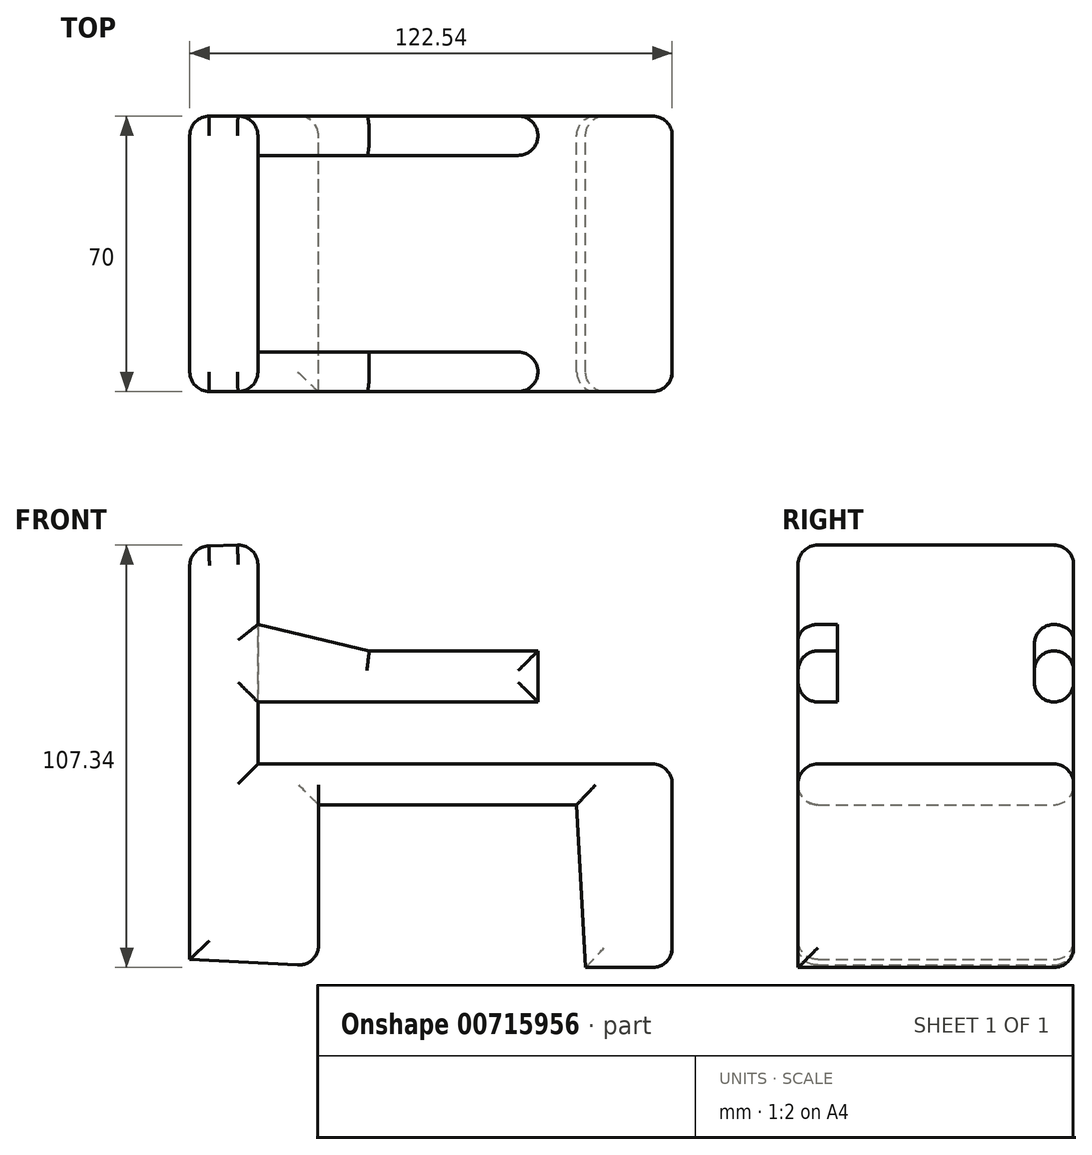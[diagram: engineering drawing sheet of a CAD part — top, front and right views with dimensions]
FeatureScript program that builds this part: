
annotation { "Feature Type Name" : "Feature", "Feature Type Description" : "" }
export const myFeature = defineFeature(function(context is Context, id is Id, definition is map)
    precondition{}
    {
        {
            var Q0;
            Q0=qCreatedBy(makeId("Front.planeOp"),FACE);
            var sketch = newSketch(context, id + "F0", { "sketchPlane" : qUnion([Q0])});
            skLineSegment(sketch, "E0", {"start": v(-51.51, 44.26) * mm, "end": v(-51.51, -11.56) * mm});
            skLineSegment(sketch, "E1", {"start": v(-51.51, -11.56) * mm, "end": v(53.74, -11.56) * mm});
            skLineSegment(sketch, "E2", {"start": v(53.74, -11.56) * mm, "end": v(53.74, -63.24) * mm});
            skLineSegment(sketch, "E3", {"start": v(53.74, -63.24) * mm, "end": v(31.75, -63.24) * mm});
            skLineSegment(sketch, "E4", {"start": v(31.75, -63.24) * mm, "end": v(29.5, -21.9) * mm});
            skLineSegment(sketch, "E5", {"start": v(29.5, -21.9) * mm, "end": v(-36.1, -21.9) * mm});
            skLineSegment(sketch, "E6", {"start": v(-36.1, -21.9) * mm, "end": v(-36.1, -62.87) * mm});
            skLineSegment(sketch, "E7", {"start": v(-36.1, -62.87) * mm, "end": v(-68.8, -61.18) * mm});
            skLineSegment(sketch, "E8", {"start": v(-68.8, -61.18) * mm, "end": v(-68.8, 43.7) * mm});
            skLineSegment(sketch, "E9", {"start": v(-68.8, 43.7) * mm, "end": v(-51.51, 44.26) * mm});
            skSolve(sketch);
        }
        {
            var Q0;
            Q0 = qSketchRegion(id + "F0", true);
            extrude(context, id + "F1", {"entities" : qUnion([Q0]), "depth" : 70 * mm, "offsetDistance" : 25 * mm});
        }
        {
            var Q0;
            Q0=qCreatedBy(makeId("Front.planeOp"),FACE);
            cPlane(context, id + "F2", {"entities" : qUnion([Q0]), "cplaneType" : CPlaneType.OFFSET, "offset" : 35 * mm, "width" : 150 * mm, "height" : 150 * mm});
        }
        {
            var Q0;
            Q0=qCreatedBy(makeId("Front.planeOp"),FACE);
            var sketch = newSketch(context, id + "F3", { "sketchPlane" : qUnion([Q0])});
            skLineSegment(sketch, "E10", {"start": v(-56.48, 25.1) * mm, "end": v(-23.21, 17.2) * mm});
            skLineSegment(sketch, "E11", {"start": v(-23.21, 17.2) * mm, "end": v(19.64, 17.2) * mm});
            skLineSegment(sketch, "E12", {"start": v(19.64, 17.2) * mm, "end": v(19.64, 4.23) * mm});
            skLineSegment(sketch, "E13", {"start": v(19.64, 4.23) * mm, "end": v(-56.48, 4.23) * mm});
            skLineSegment(sketch, "E14", {"start": v(-56.48, 4.23) * mm, "end": v(-56.48, 25.1) * mm});
            skSolve(sketch);
        }
        {
            var Q0;
            Q0 = qSketchRegion(id + "F3", true);
            extrude(context, id + "F4", {"entities" : qUnion([Q0]), "depth" : 10 * mm, "offsetDistance" : 25 * mm});
        }
        {
            var Q0;
            Q0=makeQuery(id+"F4.opExtrude","SWEPT_BODY",BODY,{"disambiguationData":[OSD([sQuery(id+"F3.wireOp",EDGE,"E10"),sQuery(id+"F3.wireOp",EDGE,"E11"),sQuery(id+"F3.wireOp",EDGE,"E12"),sQuery(id+"F3.wireOp",EDGE,"E13"),sQuery(id+"F3.wireOp",EDGE,"E14")])]});
            var Q1;
            Q1=qCreatedBy(id+"F2.planeOp",FACE);
            mirror(context, id + "F5", {"operationType" : NewBodyOperationType.ADD, "entities" : qUnion([Q0]), "mirrorPlane" : qUnion([Q1])});
        }
        {
            var Q0;
            Q0=makeQuery(id+"F1.opExtrude","CAP_EDGE",EDGE,{"disambiguationData":[OSD([sQuery(id+"F0.wireOp",EDGE,"E9")])],"isStart":true});
            var Q1;
            Q1=makeQuery(id+"F4.opExtrude","CAP_EDGE",EDGE,{"disambiguationData":[OSD([sQuery(id+"F3.wireOp",EDGE,"E10")])],"isStart":true});
            var Q2;
            Q2=makeQuery(id+"F4.opExtrude","CAP_EDGE",EDGE,{"disambiguationData":[OSD([sQuery(id+"F3.wireOp",EDGE,"E11")])],"isStart":true});
            var Q3;
            Q3=makeQuery(id+"F4.opExtrude","CAP_EDGE",EDGE,{"disambiguationData":[OSD([sQuery(id+"F3.wireOp",EDGE,"E12")])],"isStart":true});
            var Q4;
            Q4=makeQuery(id+"F4.opExtrude","CAP_EDGE",EDGE,{"disambiguationData":[OSD([sQuery(id+"F3.wireOp",EDGE,"E13")])],"isStart":true});
            var Q5;
            {var subQ0=sQuery(id+"F0.wireOp",EDGE,"E1");var subQ1=sQuery(id+"F0.wireOp",EDGE,"E0");Q5=makeQuery(id+"F5.boolean.opBoolean","SPLIT",EDGE,{"disambiguationData":[TD([makeQuery(id+"F1.opExtrude","SWEPT_FACE",FACE,{"disambiguationData":[OSD([subQ0])]})])],"derivedFrom":makeQuery(id+"F1.opExtrude","CAP_EDGE",EDGE,{"disambiguationData":[OSD([subQ1])],"isStart":true})});}
            var Q6;
            Q6=makeQuery(id+"F1.opExtrude","CAP_EDGE",EDGE,{"disambiguationData":[OSD([sQuery(id+"F0.wireOp",EDGE,"E1")])],"isStart":true});
            var Q7;
            Q7=makeQuery(id+"F1.opExtrude","CAP_EDGE",EDGE,{"disambiguationData":[OSD([sQuery(id+"F0.wireOp",EDGE,"E2")])],"isStart":true});
            var Q8;
            Q8=makeQuery(id+"F5.boolean.opBoolean","MERGE",FACE,{"derivedFrom":[makeQuery(id+"F1.opExtrude","CAP_FACE",FACE,{"disambiguationData":[OSD([sQuery(id+"F0.wireOp",EDGE,"E0"),sQuery(id+"F0.wireOp",EDGE,"E1"),sQuery(id+"F0.wireOp",EDGE,"E2"),sQuery(id+"F0.wireOp",EDGE,"E3"),sQuery(id+"F0.wireOp",EDGE,"E4"),sQuery(id+"F0.wireOp",EDGE,"E5"),sQuery(id+"F0.wireOp",EDGE,"E6"),sQuery(id+"F0.wireOp",EDGE,"E7"),sQuery(id+"F0.wireOp",EDGE,"E8"),sQuery(id+"F0.wireOp",EDGE,"E9")])],"isStart":true}),makeQuery(id+"F4.opExtrude","CAP_FACE",FACE,{"disambiguationData":[OSD([sQuery(id+"F3.wireOp",EDGE,"E10"),sQuery(id+"F3.wireOp",EDGE,"E11"),sQuery(id+"F3.wireOp",EDGE,"E12"),sQuery(id+"F3.wireOp",EDGE,"E13"),sQuery(id+"F3.wireOp",EDGE,"E14")])],"isStart":true})]});
            var Q9;
            Q9=makeQuery(id+"F1.opExtrude","CAP_EDGE",EDGE,{"disambiguationData":[OSD([sQuery(id+"F0.wireOp",EDGE,"E9")])],"isStart":false});
            var Q10;
            {var subQ0=sQuery(id+"F0.wireOp",EDGE,"E9");var subQ1=sQuery(id+"F0.wireOp",EDGE,"E0");Q10=makeQuery(id+"F5.boolean.opBoolean","SPLIT",EDGE,{"disambiguationData":[TD([makeQuery(id+"F1.opExtrude","SWEPT_FACE",FACE,{"disambiguationData":[OSD([subQ0])]})])],"derivedFrom":makeQuery(id+"F1.opExtrude","CAP_EDGE",EDGE,{"disambiguationData":[OSD([subQ1])],"isStart":false})});}
            var Q11;
            Q11=makeQuery(id+"F1.opExtrude","CAP_EDGE",EDGE,{"disambiguationData":[OSD([sQuery(id+"F0.wireOp",EDGE,"E8")])],"isStart":false});
            var Q12;
            Q12=makeQuery(id+"F1.opExtrude","CAP_EDGE",EDGE,{"disambiguationData":[OSD([sQuery(id+"F0.wireOp",EDGE,"E7")])],"isStart":false});
            var Q13;
            Q13=makeQuery(id+"F1.opExtrude","SWEPT_EDGE",EDGE,{"disambiguationData":[OSD([sQuery(id+"F0.wireOp",EDGE,"E6"),sQuery(id+"F0.wireOp",EDGE,"E7")])]});
            var Q14;
            Q14=makeQuery(id+"F1.opExtrude","CAP_EDGE",EDGE,{"disambiguationData":[OSD([sQuery(id+"F0.wireOp",EDGE,"E5")])],"isStart":false});
            var Q15;
            Q15=makeQuery(id+"F1.opExtrude","CAP_EDGE",EDGE,{"disambiguationData":[OSD([sQuery(id+"F0.wireOp",EDGE,"E4")])],"isStart":false});
            var Q16;
            Q16=makeQuery(id+"F1.opExtrude","SWEPT_EDGE",EDGE,{"disambiguationData":[OSD([sQuery(id+"F0.wireOp",EDGE,"E2"),sQuery(id+"F0.wireOp",EDGE,"E3")])]});
            var Q17;
            Q17=makeQuery(id+"F1.opExtrude","CAP_EDGE",EDGE,{"disambiguationData":[OSD([sQuery(id+"F0.wireOp",EDGE,"E2")])],"isStart":false});
            fillet(context, id + "F6", {"entities" : qUnion([Q0, Q1, Q2, Q3, Q4, Q5, Q6, Q7, Q8, Q9, Q10, Q11, Q12, Q13, Q14, Q15, Q16, Q17]), "radius" : 5 * mm, "tangentPropagation" : true, "allowEdgeOverflow" : false});
        }
        {
            var Q0;
            Q0=makeQuery(id+"F5.opPattern","COPY",EDGE,{"derivedFrom":makeQuery(id+"F4.opExtrude","CAP_EDGE",EDGE,{"disambiguationData":[OSD([sQuery(id+"F3.wireOp",EDGE,"E10")])],"isStart":true}),"instanceName":"1"});
            var Q1;
            Q1=makeQuery(id+"F5.opPattern","COPY",EDGE,{"derivedFrom":makeQuery(id+"F4.opExtrude","CAP_EDGE",EDGE,{"disambiguationData":[OSD([sQuery(id+"F3.wireOp",EDGE,"E11")])],"isStart":true}),"instanceName":"1"});
            var Q2;
            Q2=makeQuery(id+"F5.opPattern","COPY",EDGE,{"derivedFrom":makeQuery(id+"F4.opExtrude","CAP_EDGE",EDGE,{"disambiguationData":[OSD([sQuery(id+"F3.wireOp",EDGE,"E12")])],"isStart":true}),"instanceName":"1"});
            var Q3;
            Q3=makeQuery(id+"F5.opPattern","COPY",EDGE,{"derivedFrom":makeQuery(id+"F4.opExtrude","CAP_EDGE",EDGE,{"disambiguationData":[OSD([sQuery(id+"F3.wireOp",EDGE,"E12")])],"isStart":false}),"instanceName":"1"});
            var Q4;
            Q4=makeQuery(id+"F5.opPattern","COPY",EDGE,{"derivedFrom":makeQuery(id+"F4.opExtrude","CAP_EDGE",EDGE,{"disambiguationData":[OSD([sQuery(id+"F3.wireOp",EDGE,"E13")])],"isStart":true}),"instanceName":"1"});
            var Q5;
            {var subQ1=sQuery(id+"F0.wireOp",EDGE,"E1");var subQ2=sQuery(id+"F0.wireOp",EDGE,"E0");Q5=makeQuery(id+"F5.boolean.opBoolean","SPLIT",EDGE,{"disambiguationData":[TD([makeQuery(id+"F1.opExtrude","SWEPT_FACE",FACE,{"disambiguationData":[OSD([subQ1])]})])],"derivedFrom":makeQuery(id+"F1.opExtrude","CAP_EDGE",EDGE,{"disambiguationData":[OSD([subQ2])],"isStart":false})});}
            var Q6;
            Q6=makeQuery(id+"F1.opExtrude","CAP_EDGE",EDGE,{"disambiguationData":[OSD([sQuery(id+"F0.wireOp",EDGE,"E1")])],"isStart":false});
            fillet(context, id + "F7", {"entities" : qUnion([Q0, Q1, Q2, Q3, Q4, Q5, Q6]), "radius" : 5 * mm, "tangentPropagation" : true, "allowEdgeOverflow" : false});
        }
        {
            var Q0;
            Q0=makeQuery(id+"F1.opExtrude","SWEPT_EDGE",EDGE,{"disambiguationData":[OSD([sQuery(id+"F0.wireOp",EDGE,"E8"),sQuery(id+"F0.wireOp",EDGE,"E9")])]});
            var Q1;
            Q1=makeQuery(id+"F1.opExtrude","SWEPT_EDGE",EDGE,{"disambiguationData":[OSD([sQuery(id+"F0.wireOp",EDGE,"E0"),sQuery(id+"F0.wireOp",EDGE,"E9")])]});
            fillet(context, id + "F8", {"entities" : qUnion([Q0, Q1]), "radius" : 5 * mm, "tangentPropagation" : true, "allowEdgeOverflow" : false});
        }
        {
            var Q0;
            Q0=makeQuery(id+"F4.opExtrude","CAP_EDGE",EDGE,{"disambiguationData":[OSD([sQuery(id+"F3.wireOp",EDGE,"E10")])],"isStart":false});
            var Q1;
            Q1=makeQuery(id+"F4.opExtrude","CAP_EDGE",EDGE,{"disambiguationData":[OSD([sQuery(id+"F3.wireOp",EDGE,"E11")])],"isStart":false});
            var Q2;
            Q2=makeQuery(id+"F4.opExtrude","CAP_EDGE",EDGE,{"disambiguationData":[OSD([sQuery(id+"F3.wireOp",EDGE,"E12")])],"isStart":false});
            var Q3;
            Q3=makeQuery(id+"F4.opExtrude","CAP_EDGE",EDGE,{"disambiguationData":[OSD([sQuery(id+"F3.wireOp",EDGE,"E13")])],"isStart":false});
            fillet(context, id + "F9", {"entities" : qUnion([Q0, Q1, Q2, Q3]), "radius" : 5 * mm, "tangentPropagation" : true, "allowEdgeOverflow" : false});
        }
    });
